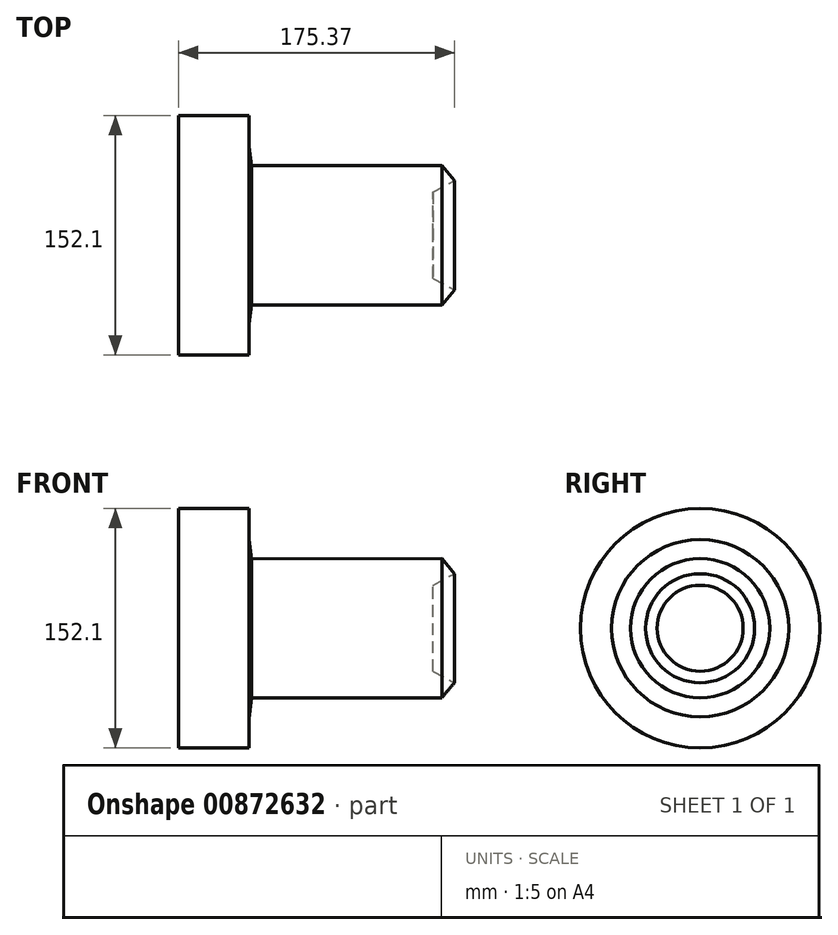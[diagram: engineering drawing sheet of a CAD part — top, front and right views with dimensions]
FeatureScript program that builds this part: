
annotation { "Feature Type Name" : "Feature", "Feature Type Description" : "" }
export const myFeature = defineFeature(function(context is Context, id is Id, definition is map)
    precondition{}
    {
        {
            var Q0;
            Q0=qCreatedBy(makeId("Front.planeOp"),FACE);
            var sketch = newSketch(context, id + "F0", { "sketchPlane" : qUnion([Q0])});
            skLineSegment(sketch, "E0", {"start": v(-67.55, 0) * mm, "end": v(-67.55, 76.05) * mm});
            skLineSegment(sketch, "E1", {"start": v(-67.55, 76.05) * mm, "end": v(-22.52, 76.05) * mm});
            skLineSegment(sketch, "E2", {"start": v(-22.52, 76.05) * mm, "end": v(-22.52, 56.27) * mm});
            skLineSegment(sketch, "E3", {"start": v(-22.52, 56.27) * mm, "end": v(-21.05, 44.15) * mm});
            skLineSegment(sketch, "E4", {"start": v(-21.05, 44.15) * mm, "end": v(99.76, 44.18) * mm});
            skLineSegment(sketch, "E5", {"start": v(99.76, 44.18) * mm, "end": v(107.82, 34.63) * mm});
            skLineSegment(sketch, "E6", {"start": v(107.82, 34.63) * mm, "end": v(94.27, 27.33) * mm});
            skLineSegment(sketch, "E7", {"start": v(94.27, 27.33) * mm, "end": v(94.27, 0) * mm});
            skLineSegment(sketch, "E8", {"start": v(94.27, 0) * mm, "end": v(-67.55, 0) * mm});
            skSolve(sketch);
        }
        {
            var Q0;
            Q0=makeQuery(id+"F0.imprint","IMPRINT",FACE,{"disambiguationData":[TD([[makeQuery(id+"F0.imprint","IMPRINT",EDGE,{"derivedFrom":sQuery(id+"F0.wireOp",EDGE,"E0")}),-1.0]])]});
            var Q1;
            Q1=sQuery(id+"F0.wireOp",EDGE,"E8");
            revolve(context, id + "F1", {"surfaceOperationType" : NewSurfaceOperationType.NEW, "entities" : qUnion([Q0]), "axis" : qUnion([Q1]), "revolveType" : RevolveType.FULL});
        }
    });
